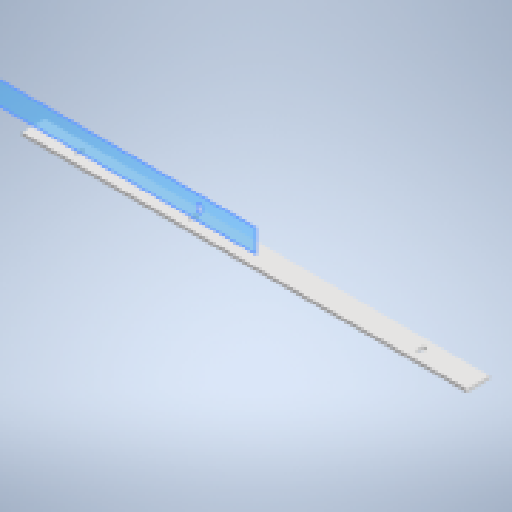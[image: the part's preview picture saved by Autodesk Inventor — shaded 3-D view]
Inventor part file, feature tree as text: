
AUTODESK INVENTOR PART (.ipt)
format: ipt  version: 2024 (Build 280153000, 153)  size: 169,472 bytes
history: native  units: mm
features: extrude x2, sketch x2, other x1
ambient origin geometry x8: Origin, YZ Plane, XZ Plane, XY Plane, X Axis, Y Axis, Z Axis, Center Point
bodies: Body1 (feature_tree)
feature tree (5):
  other  "솔리드1"
  extrude  "돌출1"  Depth=390.0mm
  extrude  "돌출2"  Depth=20.0mm
  sketch  "스케치1"
  sketch  "스케치3"
